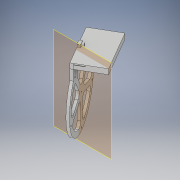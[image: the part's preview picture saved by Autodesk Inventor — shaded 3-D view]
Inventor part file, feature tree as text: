
AUTODESK INVENTOR PART (.ipt)
format: ipt  version: 2017 (Build 210142000, 142)  size: 219,648 bytes
history: native  units: in
note: dims shown in document units (in); Inventor stores cm internally (conversion verified against a paired STEP export)
features: projected_geometry x3, extrude x1, sketch x1, imported_body x1
ambient origin geometry x8: Origin, YZ Plane, XZ Plane, XY Plane, X Axis, Y Axis, Z Axis, Center Point
bodies: Solid1 (feature_tree)
feature tree (6):
  extrude  "Extrusion1"  [1 undecoded]
  sketch  "Sketch1"  dims[d0=1.25in d1=0.0in]
  projected_geometry  "Projected Loop1"
  projected_geometry  "Projected Loop2"
  projected_geometry  "Projected Loop3"
  imported_body  "Base1"
note: 1 required parameter value undecoded (feature->parameter linkage not recoverable at this tier; creation-order binding heuristic only, values carry confidence <= 0.55)
